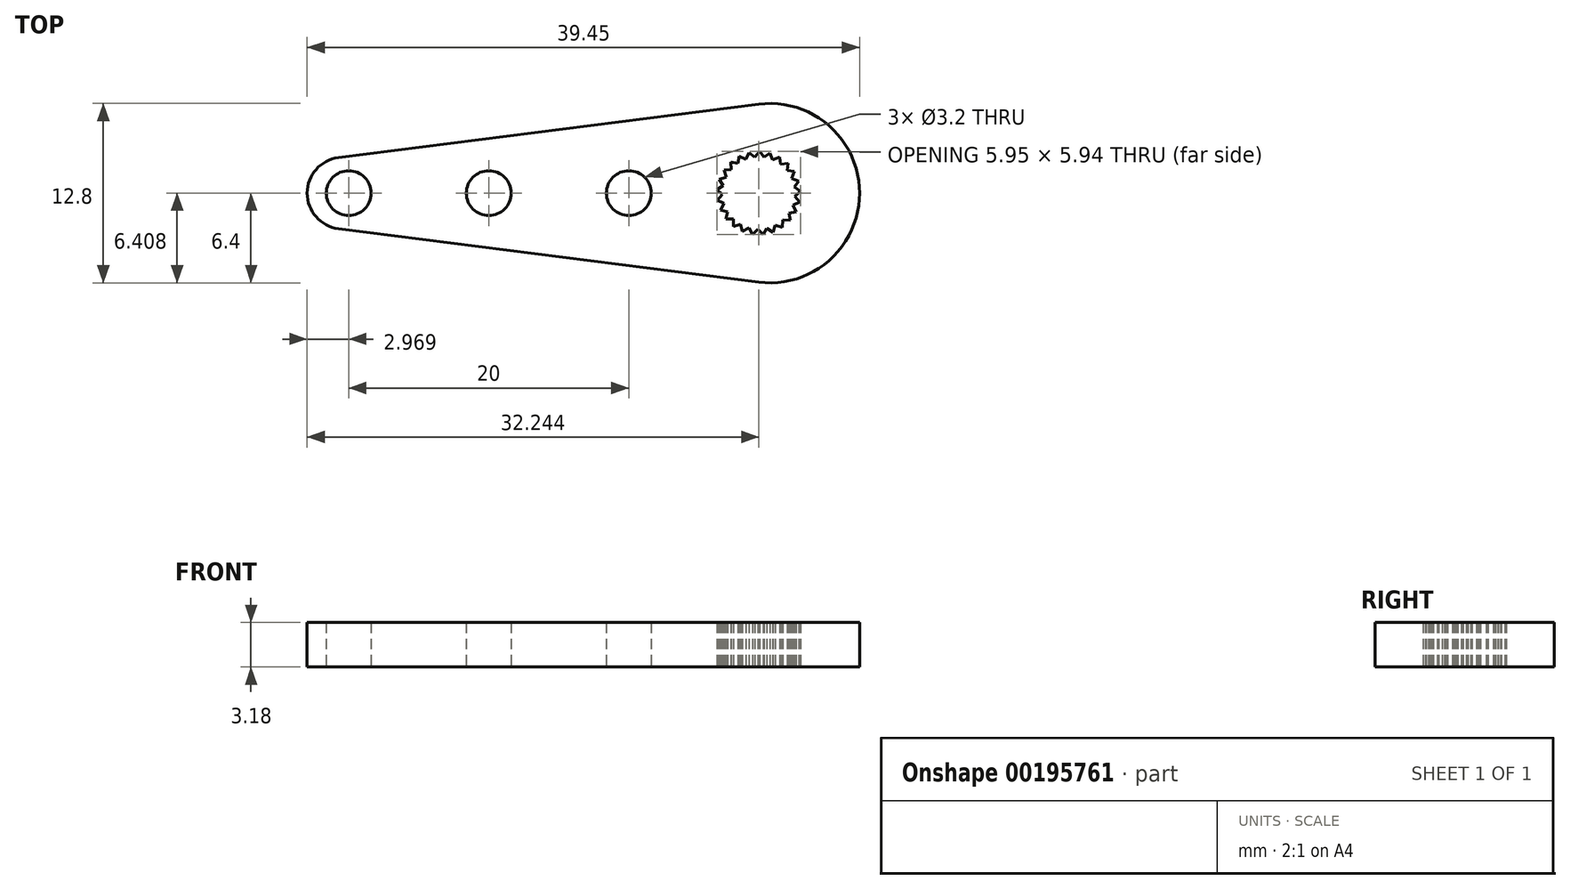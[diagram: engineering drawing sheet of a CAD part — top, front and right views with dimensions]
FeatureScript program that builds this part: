
annotation { "Feature Type Name" : "Feature", "Feature Type Description" : "" }
export const myFeature = defineFeature(function(context is Context, id is Id, definition is map)
    precondition{}
    {
        {
            var Q0;
            Q0=qCreatedBy(makeId("Top.planeOp"),FACE);
            var sketch = newSketch(context, id + "F0", { "sketchPlane" : qUnion([Q0])});
            skLineSegment(sketch, "E0", {"start": v(-2.48, 1.65) * mm, "end": v(-2.31, 1.15) * mm});
            skLineSegment(sketch, "E1", {"start": v(-2.31, 1.15) * mm, "end": v(-2.81, 0.98) * mm});
            skLineSegment(sketch, "E2.1.0", {"start": v(-2.81, 0.98) * mm, "end": v(-2.53, 0.54) * mm});
            skLineSegment(sketch, "E2.1.1", {"start": v(-2.53, 0.54) * mm, "end": v(-2.97, 0.25) * mm});
            skLineSegment(sketch, "E2.2.0", {"start": v(-2.97, 0.25) * mm, "end": v(-2.58, -0.1) * mm});
            skLineSegment(sketch, "E2.2.1", {"start": v(-2.58, -0.1) * mm, "end": v(-2.94, -0.5) * mm});
            skLineSegment(sketch, "E2.3.0", {"start": v(-2.94, -0.5) * mm, "end": v(-2.47, -0.74) * mm});
            skLineSegment(sketch, "E2.3.1", {"start": v(-2.47, -0.74) * mm, "end": v(-2.72, -1.2) * mm});
            skLineSegment(sketch, "E2.4.0", {"start": v(-2.72, -1.2) * mm, "end": v(-2.21, -1.34) * mm});
            skLineSegment(sketch, "E2.4.1", {"start": v(-2.21, -1.34) * mm, "end": v(-2.34, -1.85) * mm});
            skLineSegment(sketch, "E2.5.0", {"start": v(-2.34, -1.85) * mm, "end": v(-1.8, -1.84) * mm});
            skLineSegment(sketch, "E2.5.1", {"start": v(-1.8, -1.84) * mm, "end": v(-1.8, -2.37) * mm});
            skLineSegment(sketch, "E2.6.0", {"start": v(-1.8, -2.37) * mm, "end": v(-1.3, -2.24) * mm});
            skLineSegment(sketch, "E2.6.1", {"start": v(-1.3, -2.24) * mm, "end": v(-1.16, -2.75) * mm});
            skLineSegment(sketch, "E2.7.0", {"start": v(-1.16, -2.75) * mm, "end": v(-0.7, -2.49) * mm});
            skLineSegment(sketch, "E2.7.1", {"start": v(-0.7, -2.49) * mm, "end": v(-0.44, -2.95) * mm});
            skLineSegment(sketch, "E2.8.0", {"start": v(-0.44, -2.95) * mm, "end": v(-0.06, -2.58) * mm});
            skLineSegment(sketch, "E2.8.1", {"start": v(-0.06, -2.58) * mm, "end": v(0.3, -2.96) * mm});
            skLineSegment(sketch, "E2.9.0", {"start": v(0.3, -2.96) * mm, "end": v(0.59, -2.52) * mm});
            skLineSegment(sketch, "E2.9.1", {"start": v(0.59, -2.52) * mm, "end": v(1.04, -2.8) * mm});
            skLineSegment(sketch, "E2.10.0", {"start": v(1.04, -2.8) * mm, "end": v(1.2, -2.3) * mm});
            skLineSegment(sketch, "E2.10.1", {"start": v(1.2, -2.3) * mm, "end": v(1.7, -2.45) * mm});
            skLineSegment(sketch, "E2.11.0", {"start": v(1.7, -2.45) * mm, "end": v(1.73, -1.92) * mm});
            skLineSegment(sketch, "E2.11.1", {"start": v(1.73, -1.92) * mm, "end": v(2.25, -1.95) * mm});
            skLineSegment(sketch, "E2.12.0", {"start": v(2.25, -1.95) * mm, "end": v(2.15, -1.43) * mm});
            skLineSegment(sketch, "E2.12.1", {"start": v(2.15, -1.43) * mm, "end": v(2.67, -1.33) * mm});
            skLineSegment(sketch, "E2.13.0", {"start": v(2.67, -1.33) * mm, "end": v(2.44, -0.85) * mm});
            skLineSegment(sketch, "E2.13.1", {"start": v(2.44, -0.85) * mm, "end": v(2.91, -0.62) * mm});
            skLineSegment(sketch, "E2.14.0", {"start": v(2.91, -0.62) * mm, "end": v(2.57, -0.22) * mm});
            skLineSegment(sketch, "E2.14.1", {"start": v(2.57, -0.22) * mm, "end": v(2.98, 0.12) * mm});
            skLineSegment(sketch, "E2.15.0", {"start": v(2.98, 0.12) * mm, "end": v(2.55, 0.43) * mm});
            skLineSegment(sketch, "E2.15.1", {"start": v(2.55, 0.43) * mm, "end": v(2.85, 0.86) * mm});
            skLineSegment(sketch, "E2.16.0", {"start": v(2.85, 0.86) * mm, "end": v(2.36, 1.05) * mm});
            skLineSegment(sketch, "E2.16.1", {"start": v(2.36, 1.05) * mm, "end": v(2.55, 1.54) * mm});
            skLineSegment(sketch, "E2.17.0", {"start": v(2.55, 1.54) * mm, "end": v(2.03, 1.6) * mm});
            skLineSegment(sketch, "E2.17.1", {"start": v(2.03, 1.6) * mm, "end": v(2.09, 2.13) * mm});
            skLineSegment(sketch, "E2.18.0", {"start": v(2.09, 2.13) * mm, "end": v(1.56, 2.06) * mm});
            skLineSegment(sketch, "E2.18.1", {"start": v(1.56, 2.06) * mm, "end": v(1.5, 2.58) * mm});
            skLineSegment(sketch, "E2.19.0", {"start": v(1.5, 2.58) * mm, "end": v(1, 2.38) * mm});
            skLineSegment(sketch, "E2.19.1", {"start": v(1, 2.38) * mm, "end": v(0.8, 2.87) * mm});
            skLineSegment(sketch, "E2.20.0", {"start": v(0.8, 2.87) * mm, "end": v(0.38, 2.56) * mm});
            skLineSegment(sketch, "E2.20.1", {"start": v(0.38, 2.56) * mm, "end": v(0.07, 2.98) * mm});
            skLineSegment(sketch, "E2.21.0", {"start": v(0.07, 2.98) * mm, "end": v(-0.27, 2.57) * mm});
            skLineSegment(sketch, "E2.21.1", {"start": v(-0.27, 2.57) * mm, "end": v(-0.68, 2.9) * mm});
            skLineSegment(sketch, "E2.22.0", {"start": v(-0.68, 2.9) * mm, "end": v(-0.9, 2.42) * mm});
            skLineSegment(sketch, "E2.22.1", {"start": v(-0.9, 2.42) * mm, "end": v(-1.38, 2.64) * mm});
            skLineSegment(sketch, "E2.23.0", {"start": v(-1.38, 2.64) * mm, "end": v(-1.47, 2.12) * mm});
            skLineSegment(sketch, "E2.23.1", {"start": v(-1.47, 2.12) * mm, "end": v(-2, 2.22) * mm});
            skLineSegment(sketch, "E2.24.0", {"start": v(-2, 2.22) * mm, "end": v(-1.95, 1.69) * mm});
            skLineSegment(sketch, "E2.24.1", {"start": v(-1.95, 1.69) * mm, "end": v(-2.48, 1.65) * mm});
            skPoint(sketch, "E2.center", {"position": v(0, 0) * mm});
            skLineSegment(sketch, "E3", {"start": v(0, 6.35) * mm, "end": v(-30, 2.54) * mm});
            skLineSegment(sketch, "E4", {"start": v(0, -6.35) * mm, "end": v(-30, -2.54) * mm});
            skArc(sketch, "E5", {"start": v(-30, 2.54) * mm, "mid": v(-32.24, 0) * mm, "end": v(-30, -2.54) * mm});
            skCircle(sketch, "E6", {"center": v(-9.27, 0) * mm, "radius": 1.6 * mm});
            skCircle(sketch, "E7", {"center": v(-19.27, 0) * mm, "radius": 1.6 * mm});
            skCircle(sketch, "E8", {"center": v(-29.27, 0) * mm, "radius": 1.6 * mm});
            skArc(sketch, "E9", {"start": v(0, -6.35) * mm, "mid": v(7.2, 0) * mm, "end": v(0, 6.35) * mm});
            skSolve(sketch);
        }
        {
            var Q0;
            Q0=makeQuery(id+"F0.imprint","IMPRINT",FACE,{"disambiguationData":[TD([[makeQuery(id+"F0.imprint","IMPRINT",EDGE,{"derivedFrom":sQuery(id+"F0.wireOp",EDGE,"E0")}),-1.0]])]});
            extrude(context, id + "F1", {"entities" : qUnion([Q0]), "depth" : 3.17 * mm});
        }
    });
